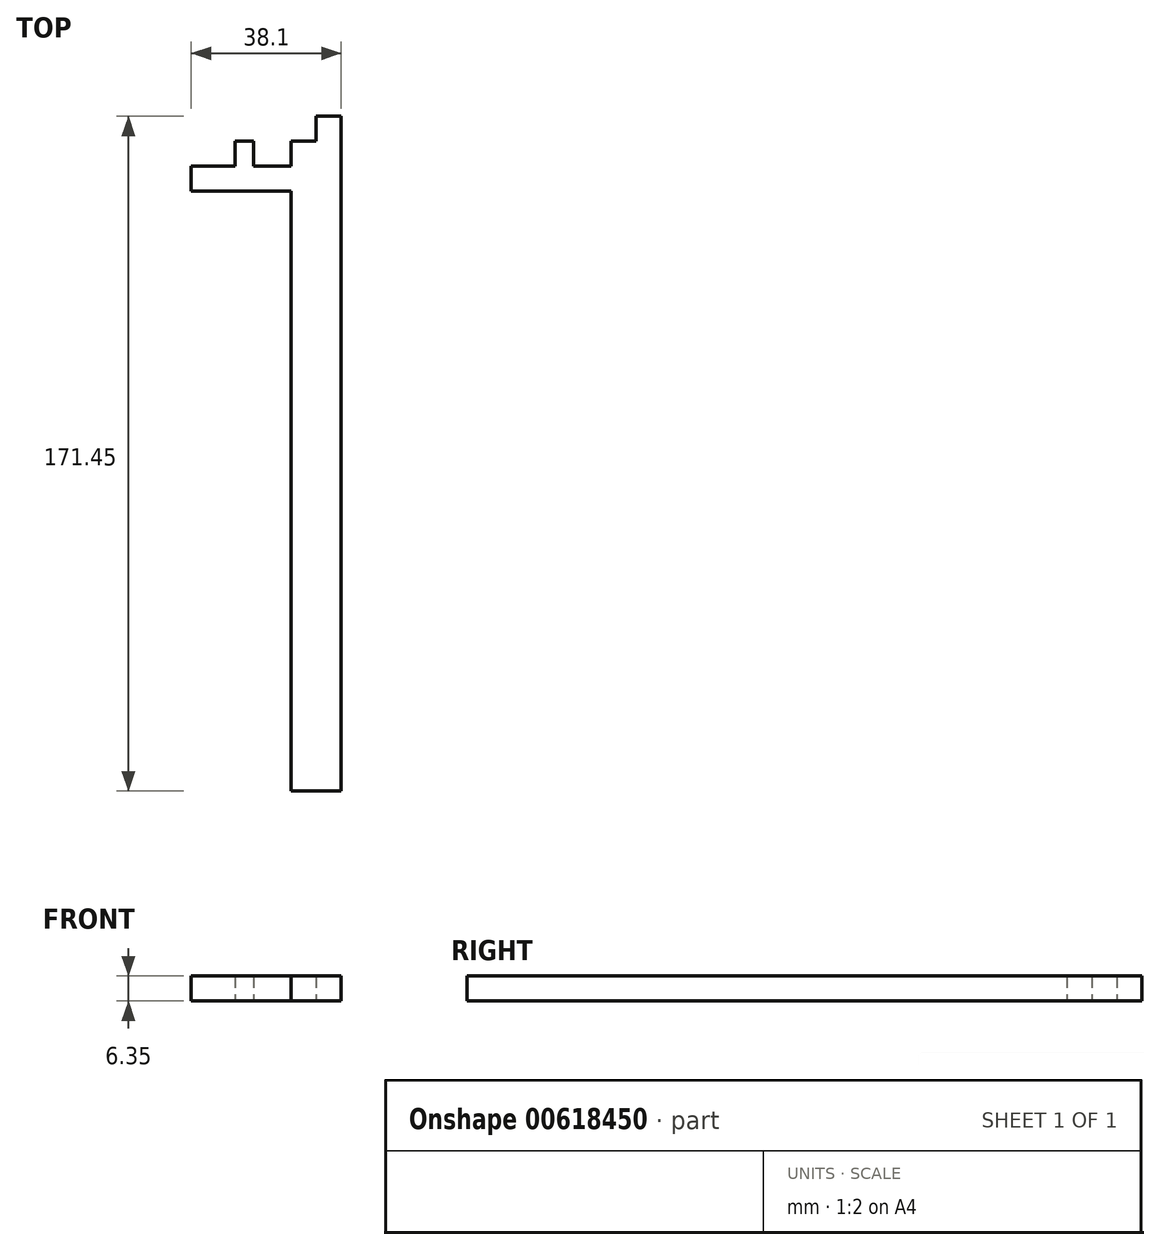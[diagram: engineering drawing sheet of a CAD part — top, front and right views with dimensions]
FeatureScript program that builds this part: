
annotation { "Feature Type Name" : "Feature", "Feature Type Description" : "" }
export const myFeature = defineFeature(function(context is Context, id is Id, definition is map)
    precondition{}
    {
        {
            var Q0;
            Q0=qCreatedBy(makeId("Top.planeOp"),FACE);
            var sketch = newSketch(context, id + "F0", { "sketchPlane" : qUnion([Q0])});
            skLineSegment(sketch, "E0.bottom", {"start": v(-46.96, 6.01) * mm, "end": v(-59.66, 6.01) * mm});
            skLineSegment(sketch, "E0.top", {"start": v(-46.96, -146.39) * mm, "end": v(-59.66, -146.39) * mm});
            skLineSegment(sketch, "E0.left", {"start": v(-46.96, 6.01) * mm, "end": v(-46.96, -146.39) * mm});
            skLineSegment(sketch, "E0.right", {"start": v(-59.66, 6.01) * mm, "end": v(-59.66, -146.39) * mm});
            skPoint(sketch, "E0.middle", {"position": v(-53.31, -70.19) * mm});
            skLineSegment(sketch, "E1.bottom", {"start": v(-46.96, 6.01) * mm, "end": v(-85.06, 6.01) * mm});
            skLineSegment(sketch, "E1.top", {"start": v(-46.96, 12.36) * mm, "end": v(-85.06, 12.36) * mm});
            skLineSegment(sketch, "E1.left", {"start": v(-46.96, 6.01) * mm, "end": v(-46.96, 12.36) * mm});
            skLineSegment(sketch, "E1.right", {"start": v(-85.06, 6.01) * mm, "end": v(-85.06, 12.36) * mm});
            skLineSegment(sketch, "E2.bottom", {"start": v(-46.96, 12.36) * mm, "end": v(-59.66, 12.36) * mm});
            skLineSegment(sketch, "E2.top", {"start": v(-46.96, 18.71) * mm, "end": v(-59.66, 18.71) * mm});
            skLineSegment(sketch, "E2.left", {"start": v(-46.96, 12.36) * mm, "end": v(-46.96, 18.71) * mm});
            skLineSegment(sketch, "E2.right", {"start": v(-59.66, 12.36) * mm, "end": v(-59.66, 18.71) * mm});
            skLineSegment(sketch, "E3.bottom", {"start": v(-46.96, 18.71) * mm, "end": v(-53.31, 18.71) * mm});
            skLineSegment(sketch, "E3.top", {"start": v(-46.96, 25.06) * mm, "end": v(-53.31, 25.06) * mm});
            skLineSegment(sketch, "E3.left", {"start": v(-46.96, 18.71) * mm, "end": v(-46.96, 25.06) * mm});
            skLineSegment(sketch, "E3.right", {"start": v(-53.31, 18.71) * mm, "end": v(-53.31, 25.06) * mm});
            skLineSegment(sketch, "E4.bottom", {"start": v(-69.19, 12.36) * mm, "end": v(-73.95, 12.36) * mm});
            skLineSegment(sketch, "E4.top", {"start": v(-69.19, 18.71) * mm, "end": v(-73.95, 18.71) * mm});
            skLineSegment(sketch, "E4.left", {"start": v(-69.19, 12.36) * mm, "end": v(-69.19, 18.71) * mm});
            skLineSegment(sketch, "E4.right", {"start": v(-73.95, 12.36) * mm, "end": v(-73.95, 18.71) * mm});
            skSolve(sketch);
        }
        {
            var Q0;
            Q0=qSketchRegion(id+"F0",true);
            extrude(context, id + "F1", {"entities" : qUnion([Q0]), "depth" : 6.35 * mm, "offsetDistance" : 25.4 * mm});
        }
    });
